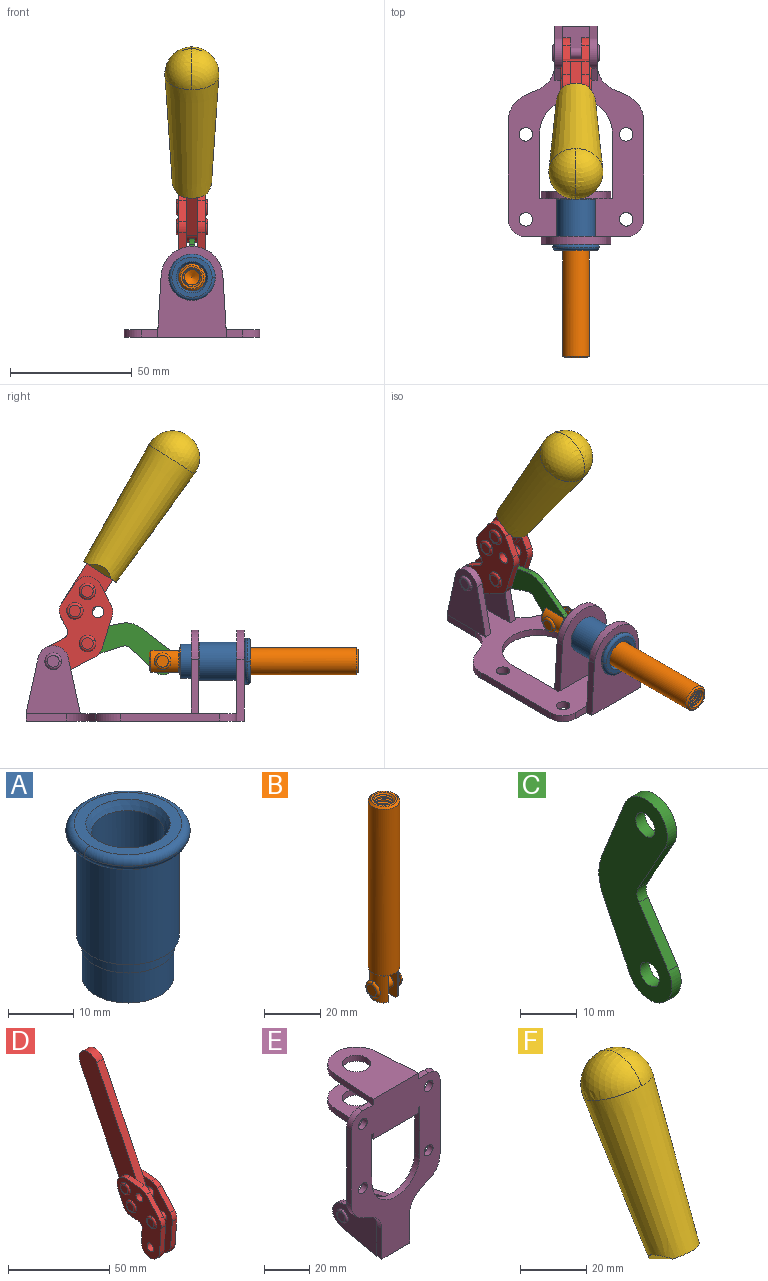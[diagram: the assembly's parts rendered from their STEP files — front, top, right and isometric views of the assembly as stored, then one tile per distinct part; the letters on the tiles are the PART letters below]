
ASSEMBLY  parts=6 mates=6
PART A: 15 faces, bbox 20.6x20.6x28.7 mm
  f0: torus R=8.26mm, axis (0,0,1), area 56.8mm2, adj f1,f10,f12
  f1: torus R=8.26mm, axis (0,0,1), area 56.8mm2, adj f0,f6,f13
  f2: cylinder r=5.59mm len=25.91mm, axis (0,0,1), area 909.6mm2, adj f3,f4
  f3: cone r=6.86mm half-angle=45deg, axis (0,0,-1), area 70.2mm2, adj f2,f14
  f4: cone r=6.47mm half-angle=30deg, axis (0,0,1), area 66.7mm2, adj f2,f13
  f5: cylinder r=7.04mm len=14.07mm, axis (0,0,1), area 252.6mm2, adj f11,f14
  f6: torus R=8.26mm, axis (0,0,1), area 56.8mm2, adj f1,f12,f13
  f7: cylinder r=7.16mm len=14.33mm, axis (0,0,1), area 91.5mm2, adj f9,f11
  f8: cylinder r=7.86mm len=18.42mm, axis (0,0,1), area 909.6mm2, adj f9,f10
  f9: plane 15.72x15.72mm, normal (0,0,-1), area 33mm2, adj f7,f8
  f10: plane 16.51x16.51mm, normal (0,0,-1), area 19.9mm2, adj f0,f8,f12
  f11: plane 14.33x14.33mm, normal (0,0,-1), area 5.7mm2, adj f5,f7
  f12: torus R=8.26mm, axis (0,0,1), area 56.8mm2, adj f0,f6,f10
  f13: plane 16.51x16.51mm, normal (0,0,1), area 82.7mm2, adj f1,f4,f6
  f14: plane 14.07x14.07mm, normal (0,0,-1), area 7.8mm2, adj f3,f5
PART B: 48 faces, bbox 12.6x11.1x86.1 mm
  f0: torus R=2.41mm, axis (-1,0,0), area 15mm2, adj f30,f32,f34
  f1: torus R=2.41mm, axis (-1,0,0), area 15mm2, adj f29,f31,f33
  f2: cylinder r=5.54mm len=72.39mm, axis (0,0,1), area 2518.5mm2, adj f3,f4,f42,f43
  f3: cone r=5.54mm half-angle=45deg, axis (0,0,1), area 7.6mm2, adj f2,f5,f41
  f4: cone r=5.54mm half-angle=45deg, axis (0,0,-1), area 34.9mm2, adj f2,f39
  f5: cylinder r=5.08mm len=11.48mm, axis (0,0,1), area 108.3mm2, adj f3,f7,f8,f41
  f6: cylinder r=2.41mm len=4.83mm, axis (-1,0,0), area 71.2mm2, adj f40,f41
  f7: cylinder r=2.41mm len=4.83mm, axis (-1,0,0), area 7.6mm2, adj f5,f34
  f8: cone r=5.08mm half-angle=45deg, axis (0,0,1), area 10.6mm2, adj f5,f37,f41
  f9: cone r=3.98mm half-angle=45deg, axis (0,0,1), area 17.6mm2, adj f27,f39,f45,f46,f47
  f10: cylinder r=2.41mm len=4.83mm, axis (-1,0,0), area 7.6mm2, adj f33,f38
  f11: cylinder r=3.2mm len=6.4mm, axis (0,0,1), area 78.4mm2, adj f12,f28,f44,f45,f47
  f12: cylinder r=3.2mm len=6.4mm, axis (0,0,1), area 10.5mm2, adj f11,f13,f45,f47
  f13: cylinder r=3.2mm len=6.4mm, axis (0,0,1), area 10.5mm2, adj f12,f14,f45,f47
  f14: cylinder r=3.2mm len=6.4mm, axis (0,0,1), area 10.5mm2, adj f13,f15,f45,f47
  f15: cylinder r=3.2mm len=6.4mm, axis (0,0,1), area 10.5mm2, adj f14,f16,f45,f47
  f16: cylinder r=3.2mm len=6.4mm, axis (0,0,1), area 10.5mm2, adj f15,f17,f45,f47
  f17: cylinder r=3.2mm len=6.4mm, axis (0,0,1), area 10.5mm2, adj f16,f18,f45,f47
  f18: cylinder r=3.2mm len=6.4mm, axis (0,0,1), area 10.5mm2, adj f17,f19,f45,f47
  f19: cylinder r=3.2mm len=6.4mm, axis (0,0,1), area 10.5mm2, adj f18,f20,f45,f47
  f20: cylinder r=3.2mm len=6.4mm, axis (0,0,1), area 10.5mm2, adj f19,f21,f45,f47
  f21: cylinder r=3.2mm len=6.4mm, axis (0,0,1), area 10.5mm2, adj f20,f22,f45,f47
  f22: cylinder r=3.2mm len=6.4mm, axis (0,0,1), area 10.5mm2, adj f21,f23,f45,f47
  f23: cylinder r=3.2mm len=6.4mm, axis (0,0,1), area 10.5mm2, adj f22,f24,f45,f47
  f24: cylinder r=3.2mm len=6.4mm, axis (0,0,1), area 10.5mm2, adj f23,f25,f45,f47
  f25: cylinder r=3.2mm len=6.4mm, axis (0,0,1), area 10.5mm2, adj f24,f26,f45,f47
  f26: cylinder r=3.2mm len=6.4mm, axis (0,0,1), area 10.5mm2, adj f25,f27,f45,f47
  f27: cylinder r=3.2mm len=6.4mm, axis (0,0,1), area 7.4mm2, adj f9,f26,f45,f47
  f28: cone r=3.2mm half-angle=60deg, axis (0,0,1), area 37.2mm2, adj f11
  f29: plane 4.83x4.83mm, normal (-1,0,0), area 18.3mm2, adj f1,f31
  f30: plane 4.83x4.83mm, normal (1,0,0), area 18.3mm2, adj f0,f32
  f31: torus R=2.41mm, axis (-1,0,0), area 15mm2, adj f1,f29,f33
  f32: torus R=2.41mm, axis (-1,0,0), area 15mm2, adj f0,f30,f34
  f33: plane 6.83x6.83mm, normal (1,0,0), area 18.3mm2, adj f1,f10,f31
  f34: plane 6.83x6.83mm, normal (-1,0,0), area 18.3mm2, adj f0,f7,f32
  f35: cone r=5.08mm half-angle=45deg, axis (0,0,1), area 10.6mm2, adj f36,f38,f40
  f36: plane 7.25x1.97mm, normal (0,0,-1), area 10mm2, adj f35,f40
  f37: plane 7.25x1.97mm, normal (0,0,-1), area 10mm2, adj f8,f41
  f38: cylinder r=5.08mm len=11.48mm, axis (0,0,1), area 108.3mm2, adj f10,f35,f40,f42
  f39: plane 9.55x9.55mm, normal (0,0,1), area 22mm2, adj f4,f9
  f40: plane 12.76x10.09mm, normal (1,0,0), area 95.7mm2, adj f6,f35,f36,f38,f42,f43
  f41: plane 12.76x10.09mm, normal (-1,0,0), area 95.7mm2, adj f3,f5,f6,f8,f37,f43
  f42: cone r=5.54mm half-angle=45deg, axis (0,0,1), area 7.6mm2, adj f2,f38,f40
  f43: plane 11.07x4.7mm, normal (0,0,-1), area 50.4mm2, adj f2,f40,f41
  f44: plane 0.89x0.62mm, normal (-1,0,0), area 0.3mm2, adj f11,f45,f46,f47
  f45: bspline ~24.8x7.63mm, area 266.6mm2, adj f9,f11,f12,f13,f14,f15,f16,f17
  f46: bspline ~24.87x7.63mm, area 73.6mm2, adj f9,f44,f45,f47
  f47: bspline ~24.98x7.63mm, area 272.5mm2, adj f9,f11,f12,f13,f14,f15,f16,f17
PART C: 12 faces, bbox 2.3x18.2x42.8 mm
  f0: cylinder r=2.4mm len=4.8mm, axis (1,0,0), area 34.9mm2, adj f4,f11
  f1: cylinder r=10.41mm len=8.47mm, axis (1,0,0), area 20.2mm2, adj f4,f9,f10,f11
  f2: cylinder r=3.05mm len=3.16mm, axis (1,0,0), area 7.7mm2, adj f4,f6,f7,f11
  f3: cylinder r=2.4mm len=4.8mm, axis (1,0,0), area 34.9mm2, adj f4,f11
  f4: plane 42.81x18.23mm, normal (-1,0,0), area 414.1mm2, adj f0,f1,f2,f3,f5,f6,f7,f8
  f5: cylinder r=5.54mm len=10.67mm, axis (1,0,0), area 41.8mm2, adj f4,f6,f10,f11
  f6: plane 11.66x6.53mm, normal (0,-0.87,-0.49), area 30.9mm2, adj f2,f4,f5,f11
  f7: plane 11.17x7.33mm, normal (0,-0.84,0.55), area 30.9mm2, adj f2,f4,f8,f11
  f8: cylinder r=5.54mm len=10.51mm, axis (1,0,0), area 41.8mm2, adj f4,f7,f9,f11
  f9: plane 13.67x6.67mm, normal (0,0.9,-0.44), area 35.1mm2, adj f1,f4,f8,f11
  f10: plane 14.1x5.7mm, normal (0,0.93,0.37), area 35.1mm2, adj f1,f4,f5,f11
  f11: plane 42.81x18.23mm, normal (1,0,0), area 414.1mm2, adj f0,f1,f2,f3,f5,f6,f7,f8
PART D: 59 faces, bbox 12.9x60.2x99.6 mm
  f0: torus R=2.39mm, axis (-1,0,0), area 14.9mm2, adj f20,f43,f51
  f1: torus R=2.39mm, axis (-1,0,0), area 14.9mm2, adj f19,f42,f51
  f2: torus R=2.39mm, axis (-1,0,0), area 14.9mm2, adj f18,f35,f51
  f3: torus R=2.39mm, axis (-1,0,0), area 14.9mm2, adj f14,f17,f23
  f4: torus R=2.39mm, axis (-1,0,0), area 14.9mm2, adj f13,f16,f23
  f5: torus R=2.39mm, axis (-1,0,0), area 14.9mm2, adj f12,f15,f23
  f6: cylinder r=2.39mm len=4.78mm, axis (1,0,0), area 46.5mm2, adj f48,f50,f51
  f7: cylinder r=2.39mm len=4.78mm, axis (1,0,0), area 46.5mm2, adj f50,f51
  f8: cylinder r=6.35mm len=12.68mm, axis (1,0,0), area 61.8mm2, adj f38,f39,f50,f51
  f9: cylinder r=2.39mm len=4.78mm, axis (-1,0,0), area 70.5mm2, adj f46,f50
  f10: cylinder r=2.39mm len=4.78mm, axis (-1,0,0), area 46.5mm2, adj f23,f45,f46
  f11: cylinder r=2.39mm len=4.78mm, axis (-1,0,0), area 46.5mm2, adj f23,f46
  f12: plane 4.78x4.78mm, normal (1,0,0), area 17.9mm2, adj f5,f15
  f13: plane 4.78x4.78mm, normal (1,0,0), area 17.9mm2, adj f4,f16
  f14: plane 4.78x4.78mm, normal (1,0,0), area 17.9mm2, adj f3,f17
  f15: torus R=2.39mm, axis (-1,0,0), area 14.9mm2, adj f5,f12,f23
  f16: torus R=2.39mm, axis (-1,0,0), area 14.9mm2, adj f4,f13,f23
  f17: torus R=2.39mm, axis (-1,0,0), area 14.9mm2, adj f3,f14,f23
  f18: plane 4.78x4.78mm, normal (-1,0,0), area 17.9mm2, adj f2,f35
  f19: plane 4.78x4.78mm, normal (-1,0,0), area 17.9mm2, adj f1,f42
  f20: plane 4.78x4.78mm, normal (-1,0,0), area 17.9mm2, adj f0,f43
  f21: plane 2.26x0.2mm, normal (1,0,0), area 0.2mm2, adj f31,f44
  f22: plane 2.26x0.2mm, normal (-1,0,0), area 0.2mm2, adj f41,f44
  f23: plane 39.37x30.77mm, normal (1,0,0), area 565.5mm2, adj f3,f4,f5,f10,f11,f15,f16,f17
  f24: cylinder r=6.1mm len=4.15mm, axis (-1,0,0), area 14.7mm2, adj f23,f25,f32,f46
  f25: plane 10.25x9.01mm, normal (0,-0.75,0.66), area 42.3mm2, adj f23,f24,f26,f46
  f26: cylinder r=6.35mm len=4.64mm, axis (-1,0,0), area 15.6mm2, adj f23,f25,f27,f46
  f27: plane 15.84x3.1mm, normal (0,-1,-0.07), area 49.2mm2, adj f23,f26,f28,f46
  f28: cylinder r=6.35mm len=12.68mm, axis (-1,0,0), area 61.8mm2, adj f23,f27,f29,f46
  f29: plane 8.11x3.1mm, normal (0,1,0.07), area 25.2mm2, adj f23,f28,f30,f46
  f30: cylinder r=3.05mm len=3.25mm, axis (-1,0,0), area 14.8mm2, adj f23,f29,f31,f46
  f31: plane 5.99x3.1mm, normal (0,0.07,-1), area 18.6mm2, adj f21,f23,f30,f44,f46
  f32: plane 9.5x3.1mm, normal (0,-0.07,1), area 29.5mm2, adj f23,f24,f33,f46,f47
  f33: cylinder r=6.1mm len=8.63mm, axis (-1,0,0), area 39.1mm2, adj f23,f32,f34,f47
  f34: plane 8.65x3.96mm, normal (0,0.91,-0.42), area 29.5mm2, adj f23,f33,f44,f47
  f35: torus R=2.39mm, axis (-1,0,0), area 14.9mm2, adj f2,f18,f51
  f36: plane 10.25x9.01mm, normal (0,-0.75,0.66), area 42.3mm2, adj f37,f49,f50,f51
  f37: cylinder r=6.35mm len=4.64mm, axis (1,0,0), area 15.6mm2, adj f36,f38,f50,f51
  f38: plane 15.84x3.1mm, normal (0,-1,-0.07), area 49.2mm2, adj f8,f37,f50,f51
  f39: plane 8.11x3.1mm, normal (0,1,0.07), area 25.2mm2, adj f8,f40,f50,f51
  f40: cylinder r=3.05mm len=3.25mm, axis (1,0,0), area 14.8mm2, adj f39,f41,f50,f51
  f41: plane 5.99x3.1mm, normal (0,0.07,-1), area 18.6mm2, adj f22,f40,f44,f50,f51
  f42: torus R=2.39mm, axis (-1,0,0), area 14.9mm2, adj f1,f19,f51
  f43: torus R=2.39mm, axis (-1,0,0), area 14.9mm2, adj f0,f20,f51
  f44: cylinder r=6.35mm len=12.12mm, axis (-1,0,0), area 128.9mm2, adj f21,f22,f23,f31,f34,f41,f46,f47
  f45: plane 2.65x1.35mm, normal (1,0,0), area 1mm2, adj f10,f55
  f46: plane 39.08x20.42mm, normal (-1,0,0), area 412.5mm2, adj f9,f10,f11,f24,f25,f26,f27,f28
  f47: plane 77.62x39.82mm, normal (1,0,0), area 850mm2, adj f32,f33,f34,f44,f53,f54,f55
  f48: plane 2.65x1.35mm, normal (-1,0,0), area 1mm2, adj f6,f55
  f49: cylinder r=6.1mm len=4.15mm, axis (1,0,0), area 14.7mm2, adj f36,f50,f51,f56
  f50: plane 39.08x20.42mm, normal (1,0,0), area 412.5mm2, adj f6,f7,f8,f9,f36,f37,f38,f39
  f51: plane 39.37x30.77mm, normal (-1,0,0), area 565.5mm2, adj f0,f1,f2,f6,f7,f8,f35,f36
  f52: plane 8.65x3.96mm, normal (0,0.91,-0.42), area 29.5mm2, adj f44,f51,f57,f58
  f53: plane 68.49x33.4mm, normal (0,0.9,-0.44), area 358.1mm2, adj f44,f47,f54,f58
  f54: cylinder r=6.35mm len=12.06mm, axis (1,0,0), area 93.7mm2, adj f47,f53,f55,f58
  f55: plane 68.49x33.4mm, normal (0,-0.9,0.44), area 358.1mm2, adj f44,f45,f46,f47,f48,f50,f54,f58
  f56: plane 9.5x3.1mm, normal (0,-0.07,1), area 29.5mm2, adj f49,f50,f51,f57,f58
  f57: cylinder r=6.1mm len=8.63mm, axis (1,0,0), area 39.1mm2, adj f51,f52,f56,f58
  f58: plane 77.62x39.82mm, normal (-1,0,0), area 850mm2, adj f44,f52,f53,f54,f55,f56,f57
PART E: 55 faces, bbox 55.7x37.4x89.8 mm
  f0: torus R=2.41mm, axis (-1,0,0), area 15mm2, adj f11,f15,f25
  f1: torus R=2.41mm, axis (-1,0,0), area 15mm2, adj f10,f12,f22
  f2: cylinder r=2.78mm len=5.56mm, axis (0,-1,0), area 54.2mm2, adj f30,f54
  f3: cylinder r=14.99mm len=29.97mm, axis (0,-1,0), area 145.9mm2, adj f30,f49,f53,f54
  f4: cylinder r=2.78mm len=5.56mm, axis (0,-1,0), area 54.2mm2, adj f30,f54
  f5: cylinder r=2.78mm len=5.56mm, axis (0,-1,0), area 54.2mm2, adj f30,f54
  f6: cylinder r=2.78mm len=5.56mm, axis (0,-1,0), area 54.2mm2, adj f30,f54
  f7: cylinder r=6.35mm len=12.7mm, axis (0,0,1), area 123.6mm2, adj f27,f51
  f8: cylinder r=6.35mm len=12.7mm, axis (0,0,-1), area 124.7mm2, adj f21,f35
  f9: cylinder r=2.41mm len=11.18mm, axis (-1,0,0), area 169.4mm2, adj f16,f19
  f10: plane 4.83x4.83mm, normal (1,0,0), area 18.3mm2, adj f1,f12
  f11: plane 4.83x4.83mm, normal (-1,0,0), area 18.3mm2, adj f0,f15
  f12: torus R=2.41mm, axis (-1,0,0), area 15mm2, adj f1,f10,f22
  f13: cylinder r=6.35mm len=12.41mm, axis (1,0,0), area 53.4mm2, adj f18,f19,f22,f23
  f14: cylinder r=6.35mm len=12.41mm, axis (-1,0,0), area 53.4mm2, adj f16,f17,f24,f25
  f15: torus R=2.41mm, axis (-1,0,0), area 15mm2, adj f0,f11,f25
  f16: plane 27.86x22.35mm, normal (1,0,0), area 425.4mm2, adj f9,f14,f17,f24,f30
  f17: plane 22.86x4.97mm, normal (0,0.21,0.98), area 72.5mm2, adj f14,f16,f25,f30
  f18: plane 22.86x4.97mm, normal (0,0.21,0.98), area 72.5mm2, adj f13,f19,f22,f30
  f19: plane 27.86x22.35mm, normal (-1,0,0), area 425.4mm2, adj f9,f13,f18,f23,f30
  f20: cylinder r=12.7mm len=25.35mm, axis (0,0,-1), area 119.8mm2, adj f21,f34,f35,f36
  f21: plane 34.21x28.07mm, normal (0,0,-1), area 702.4mm2, adj f8,f20,f30,f34,f36
  f22: plane 27.96x22.45mm, normal (1,0,0), area 407.2mm2, adj f1,f12,f13,f18,f23,f30,f42,f43
  f23: plane 22.86x4.97mm, normal (0,0.21,-0.98), area 72.5mm2, adj f13,f19,f22,f44
  f24: plane 22.86x4.97mm, normal (0,0.21,-0.98), area 72.5mm2, adj f14,f16,f25,f44
  f25: plane 27.86x22.35mm, normal (-1,0,0), area 407.1mm2, adj f0,f14,f15,f17,f24,f30,f45,f46
  f26: plane 3.1x0.95mm, normal (0,0,-1), area 2.7mm2, adj f30,f49,f50,f54
  f27: plane 34.21x28.07mm, normal (0,0,1), area 702.4mm2, adj f7,f28,f30,f50,f52
  f28: cylinder r=12.7mm len=25.35mm, axis (0,0,1), area 118.8mm2, adj f27,f50,f51,f52
  f29: plane 3.1x0.95mm, normal (0,0,-1), area 2.7mm2, adj f30,f52,f53,f54
  f30: plane 86.54x55.63mm, normal (0,1,0), area 2362.9mm2, adj f2,f3,f4,f5,f6,f16,f17,f18
  f31: plane 40.56x3.1mm, normal (-1,0,0), area 125.7mm2, adj f30,f32,f48,f54
  f32: cylinder r=7.11mm len=7.11mm, axis (0,-1,0), area 34.6mm2, adj f30,f31,f33,f54
  f33: plane 6.67x3.1mm, normal (0,0,1), area 20.4mm2, adj f30,f32,f34,f54
  f34: plane 25.39x3.13mm, normal (-1,0.06,0), area 79.5mm2, adj f20,f21,f33,f35,f54
  f35: plane 37.31x28.45mm, normal (0,0,1), area 789.9mm2, adj f8,f20,f34,f36,f54
  f36: plane 25.39x3.13mm, normal (1,0.06,0), area 79.5mm2, adj f20,f21,f35,f37,f54
  f37: plane 6.67x3.1mm, normal (0,0,1), area 20.4mm2, adj f30,f36,f38,f54
  f38: cylinder r=7.11mm len=7.11mm, axis (0,-1,0), area 34.6mm2, adj f30,f37,f39,f54
  f39: plane 40.56x3.1mm, normal (1,0,0), area 125.7mm2, adj f30,f38,f40,f54
  f40: cylinder r=11.18mm len=10.16mm, axis (0,-1,0), area 39.5mm2, adj f30,f39,f41,f54
  f41: plane 6.09x3.1mm, normal (0.42,0,-0.91), area 20.8mm2, adj f30,f40,f42,f54
  f42: cylinder r=11.18mm len=9.41mm, axis (0,-1,0), area 37.2mm2, adj f22,f30,f41,f43,f54
  f43: plane 16.5x3.1mm, normal (1,0,0), area 51.1mm2, adj f22,f42,f44,f54
  f44: plane 17.37x3.1mm, normal (0,0,-1), area 53.8mm2, adj f23,f24,f30,f43,f45,f54
  f45: plane 16.5x3.1mm, normal (-1,0,0), area 51.1mm2, adj f25,f44,f46,f54
  f46: cylinder r=11.18mm len=9.41mm, axis (0,-1,0), area 37.2mm2, adj f25,f30,f45,f47,f54
  f47: plane 6.09x3.1mm, normal (-0.42,0,-0.91), area 20.8mm2, adj f30,f46,f48,f54
  f48: cylinder r=11.18mm len=10.16mm, axis (0,-1,0), area 39.5mm2, adj f30,f31,f47,f54
  f49: plane 26.54x3.1mm, normal (-1,0,0), area 82.3mm2, adj f3,f26,f30,f54
  f50: plane 25.39x3.1mm, normal (1,0.06,0), area 78.8mm2, adj f26,f27,f28,f51,f54
  f51: plane 37.31x28.45mm, normal (0,0,-1), area 789.9mm2, adj f7,f28,f50,f52,f54
  f52: plane 25.39x3.1mm, normal (-1,0.06,0), area 78.8mm2, adj f27,f28,f29,f51,f54
  f53: plane 26.54x3.1mm, normal (1,0,0), area 82.3mm2, adj f3,f29,f30,f54
  f54: plane 89.66x55.63mm, normal (0,-1,0), area 2678.5mm2, adj f2,f3,f4,f5,f6,f26,f29,f31
PART F: 11 faces, bbox 22.3x42.6x64.5 mm
  f0: sphere r=11.13mm, area 411.4mm2, adj f1,f8
  f1: cone r=11.11mm half-angle=3.3deg, axis (0,0.44,0.9), area 3251.8mm2, adj f0,f7,f8,f9,f10
  f2: cylinder r=6.16mm len=11.7mm, axis (1,0,0), area 89.5mm2, adj f3,f4,f5,f6
  f3: plane 60.23x36.75mm, normal (-1,0,0), area 763.6mm2, adj f2,f4,f6,f10
  f4: plane 51.37x25.05mm, normal (0,0.9,-0.44), area 264.2mm2, adj f2,f3,f5,f10
  f5: plane 60.23x36.75mm, normal (1,0,0), area 763.6mm2, adj f2,f4,f6,f10
  f6: plane 51.37x25.05mm, normal (0,-0.9,0.44), area 264.2mm2, adj f2,f3,f5,f10
  f7: plane 9.95x5.95mm, normal (0.71,-0.31,-0.64), area 25.8mm2, adj f1,f10
  f8: sphere r=11.13mm, area 411.4mm2, adj f0,f1
  f9: plane 9.95x5.95mm, normal (-0.71,-0.31,-0.64), area 25.8mm2, adj f1,f10
  f10: plane 14.27x11.38mm, normal (0,-0.44,-0.9), area 106.7mm2, adj f1,f3,f4,f5,f6,f7,f9
PLACE A rot(axis=(1,0,0),90deg) t=(0,1.23,0)mm
PLACE B rot(axis=(1,0,0),90deg) t=(0,3.81,0)mm
PLACE C rot(axis=(1,0,0),105.3deg) t=(0,9.76,4.96)mm
PLACE D rot(axis=(1,0,0),58.6deg) t=(0,-6.89,20.35)mm
PLACE E rot(axis=(1,0,0),90deg) t=(0,1.23,0)mm fixed
PLACE F rot(axis=(1,0,0),58.6deg) t=(-0.04,-6.89,20.35)mm
MATE fastened F.f2 <-> D.f54  axis (1,0,0) through (-2.35,-16.59,109.52)mm
MATE revolute E.f0 <-> D.f7  axis (-1,0,0) through (0,33.32,24.61)mm
MATE revolute C.f5 <-> B.f6  axis (1,0,0) through (0,-11.66,24.61)mm
MATE fastened E.f7 <-> A.f2  axis (0,-1,0) through (0,-45.16,24.61)mm
MATE slider B.f2 <-> A.f2  axis (0,-1,0) through (0,-54.97,24.61)mm
MATE revolute C.f3 <-> D.f4  axis (1,0,0) through (0,19.23,31.93)mm
